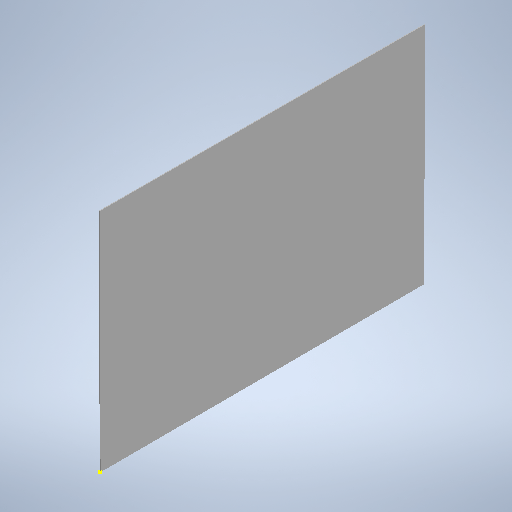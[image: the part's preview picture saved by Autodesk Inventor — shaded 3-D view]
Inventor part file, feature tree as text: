
AUTODESK INVENTOR PART (.ipt)
format: ipt  version: 2025.2 (Build 292293000, 293)  size: 567,808 bytes
history: native  units: mm
features: other x9, sketch x2, extrude x1
ambient origin geometry x8: Origin, YZ Plane, XZ Plane, XY Plane, X Axis, Y Axis, Z Axis, Center Point
bodies: Body1 (feature_tree)
feature tree (12):
  other  "ソリッド1"
  extrude  "押し出し1"  Depth=10.0mm TaperAngle=0.0deg
  sketch  "スケッチ3"
  sketch  "スケッチ1"
  other  "イメージ2"
  other  "イメージ3"
  other  "イメージ4"
  other  "イメージ5"
  other  "イメージ6"
  other  "イメージ7"
  other  "イメージ8"
  other  "イメージ9"
